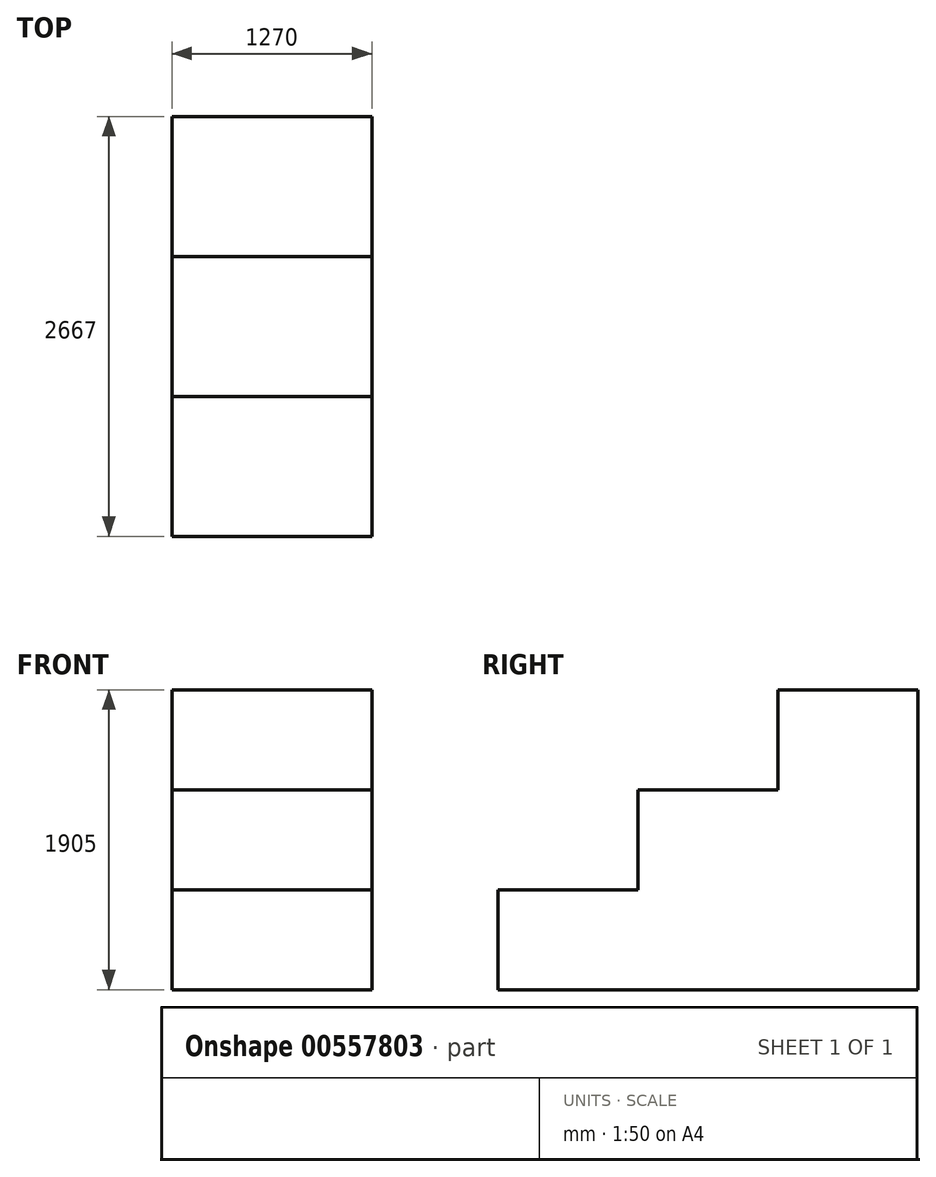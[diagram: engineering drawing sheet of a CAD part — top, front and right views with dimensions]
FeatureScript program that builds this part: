
annotation { "Feature Type Name" : "Feature", "Feature Type Description" : "" }
export const myFeature = defineFeature(function(context is Context, id is Id, definition is map)
    precondition{}
    {
        {
            var Q0;
            Q0=qCreatedBy(makeId("Right.planeOp"),FACE);
            var sketch = newSketch(context, id + "F0", { "sketchPlane" : qUnion([Q0])});
            skLineSegment(sketch, "E0", {"start": v(-474.48, -136.09) * mm, "end": v(2192.52, -136.09) * mm});
            skLineSegment(sketch, "E1", {"start": v(2192.52, -136.09) * mm, "end": v(2192.52, 1768.91) * mm});
            skLineSegment(sketch, "E2", {"start": v(2192.52, 1768.91) * mm, "end": v(1303.52, 1768.91) * mm});
            skLineSegment(sketch, "E3", {"start": v(1303.52, 1768.91) * mm, "end": v(1303.52, 1133.91) * mm});
            skLineSegment(sketch, "E4", {"start": v(1303.52, 1133.91) * mm, "end": v(414.52, 1133.91) * mm});
            skLineSegment(sketch, "E5", {"start": v(414.52, 1133.91) * mm, "end": v(414.52, 498.91) * mm});
            skLineSegment(sketch, "E6", {"start": v(414.52, 498.91) * mm, "end": v(-474.48, 498.91) * mm});
            skLineSegment(sketch, "E7", {"start": v(-474.48, 498.91) * mm, "end": v(-474.48, -136.09) * mm});
            skSolve(sketch);
        }
        {
            var Q0;
            Q0 = qSketchRegion(id + "F0", true);
            extrude(context, id + "F1", {"entities" : qUnion([Q0]), "depth" : 1270 * mm, "offsetDistance" : 25.4 * mm});
        }
    });
